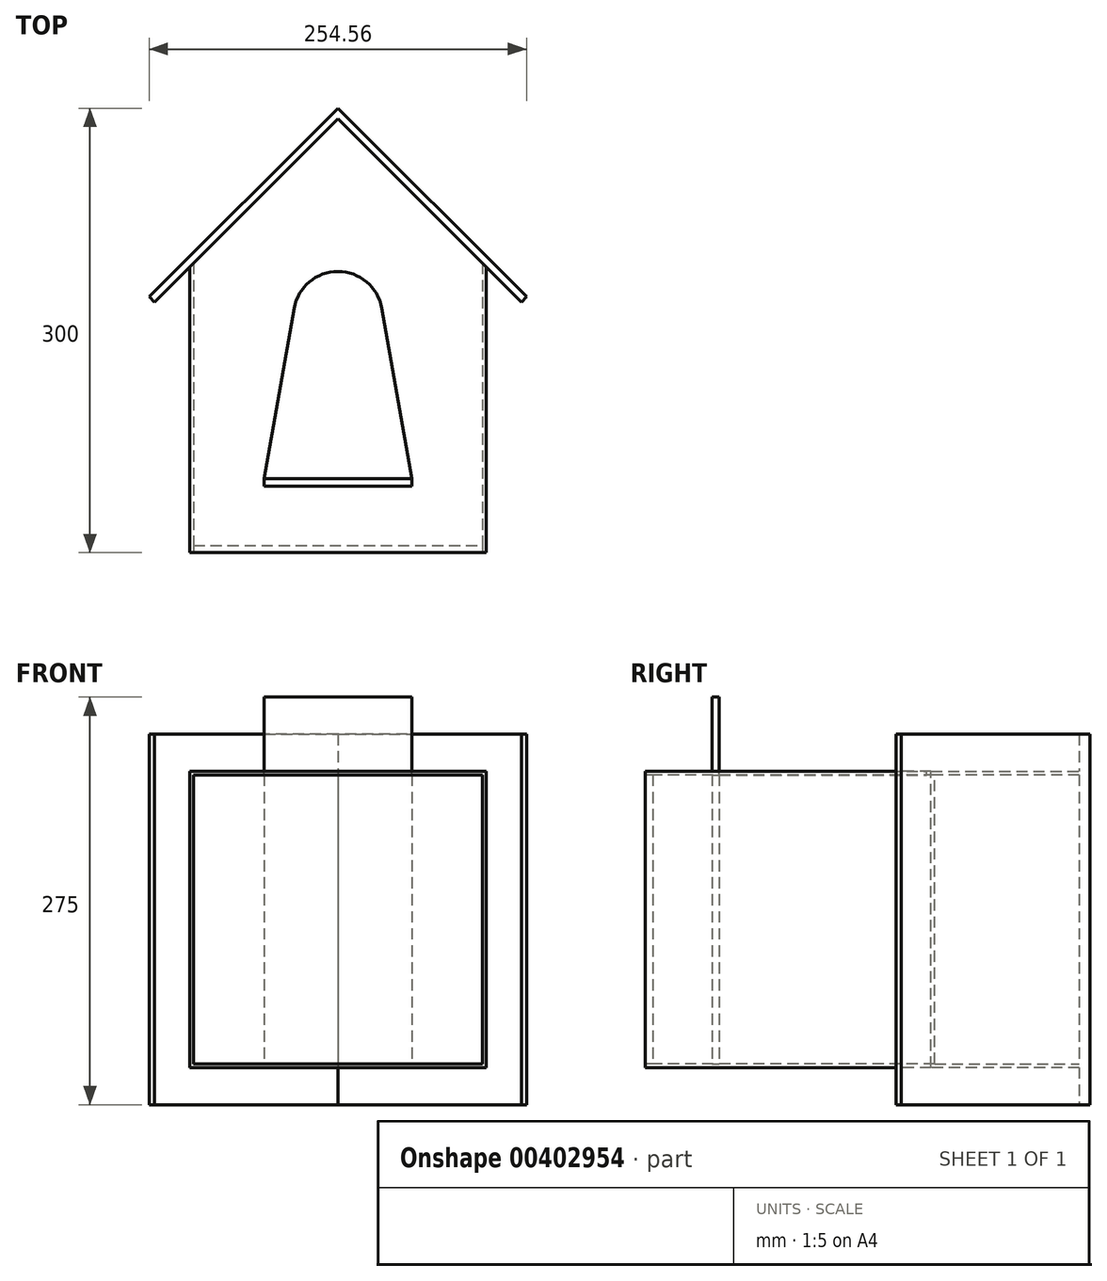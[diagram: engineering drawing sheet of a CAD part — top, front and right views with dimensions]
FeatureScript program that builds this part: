
annotation { "Feature Type Name" : "Feature", "Feature Type Description" : "" }
export const myFeature = defineFeature(function(context is Context, id is Id, definition is map)
    precondition{}
    {
        {
            var Q0;
            Q0=qCreatedBy(makeId("Top.planeOp"),FACE);
            var sketch = newSketch(context, id + "F0", { "sketchPlane" : qUnion([Q0])});
            skLineSegment(sketch, "E0.bottom", {"start": v(0, 0) * mm, "end": v(200, 0) * mm});
            skLineSegment(sketch, "E0.left", {"start": v(0, 200) * mm, "end": v(0, 0) * mm});
            skLineSegment(sketch, "E0.right", {"start": v(200, 200) * mm, "end": v(200, 0) * mm});
            skLineSegment(sketch, "E1", {"start": v(0, 200) * mm, "end": v(100, 300) * mm});
            skLineSegment(sketch, "E2", {"start": v(100, 300) * mm, "end": v(200, 200) * mm});
            skLineSegment(sketch, "E3", {"start": v(100, 300) * mm, "end": v(100, 0) * mm, "construction": true});
            skSolve(sketch);
        }
        {
            var Q0;
            Q0 = qSketchRegion(id + "F0", true);
            extrude(context, id + "F1", {"entities" : qUnion([Q0]), "depth" : 200 * mm});
        }
        {
            var Q0;
            Q0=makeQuery(id+"F1.opExtrude","SWEPT_FACE",FACE,{"disambiguationData":[OSD([sQuery(id+"F0.wireOp",EDGE,"E0.bottom")])]});
            shell(context, id + "F2", {"entities" : qUnion([Q0]), "thickness" : 2.5 * mm});
        }
        {
            var Q0;
            Q0=makeQuery(id+"F1.opExtrude","CAP_FACE",FACE,{"disambiguationData":[OSD([sQuery(id+"F0.wireOp",EDGE,"E0.bottom"),sQuery(id+"F0.wireOp",EDGE,"E0.left"),sQuery(id+"F0.wireOp",EDGE,"E0.right"),sQuery(id+"F0.wireOp",EDGE,"E1"),sQuery(id+"F0.wireOp",EDGE,"E2")])],"isStart":false});
            var sketch = newSketch(context, id + "F3", { "sketchPlane" : qUnion([Q0])});
            skLineSegment(sketch, "E4", {"start": v(100, 300) * mm, "end": v(-27.28, 172.72) * mm});
            skLineSegment(sketch, "E5", {"start": v(-27.28, 172.72) * mm, "end": v(-23.74, 169.19) * mm});
            skLineSegment(sketch, "E6", {"start": v(-23.74, 169.19) * mm, "end": v(100, 292.93) * mm});
            skLineSegment(sketch, "E7", {"start": v(100, 292.93) * mm, "end": v(223.74, 169.19) * mm});
            skLineSegment(sketch, "E8", {"start": v(223.74, 169.19) * mm, "end": v(227.28, 172.72) * mm});
            skLineSegment(sketch, "E9", {"start": v(227.28, 172.72) * mm, "end": v(100, 300) * mm});
            skSolve(sketch);
        }
        {
            var Q0;
            Q0 = qSketchRegion(id + "F3", true);
            extrude(context, id + "F4", {"entities" : qUnion([Q0]), "operationType" : NewBodyOperationType.ADD, "depth" : 25 * mm, "hasSecondDirection" : true, "secondDirectionOppositeDirection" : true, "secondDirectionDepth" : 225 * mm});
        }
        {
            var Q0;
            Q0=makeQuery(id+"F1.opExtrude","SWEPT_FACE",FACE,{"disambiguationData":[OSD([sQuery(id+"F0.wireOp",EDGE,"E0.bottom")])]});
            var sketch = newSketch(context, id + "F5", { "sketchPlane" : qUnion([Q0])});
            skLineSegment(sketch, "E10.bottom", {"start": v(2.5, 197.5) * mm, "end": v(197.5, 197.5) * mm});
            skLineSegment(sketch, "E10.top", {"start": v(2.5, 2.5) * mm, "end": v(197.5, 2.5) * mm});
            skLineSegment(sketch, "E10.left", {"start": v(2.5, 197.5) * mm, "end": v(2.5, 2.5) * mm});
            skLineSegment(sketch, "E10.right", {"start": v(197.5, 197.5) * mm, "end": v(197.5, 2.5) * mm});
            skSolve(sketch);
        }
        {
            var Q0;
            Q0 = qSketchRegion(id + "F5", true);
            extrude(context, id + "F6", {"entities" : qUnion([Q0]), "oppositeDirection" : true, "depth" : 5 * mm});
        }
        {
            var Q0;
            Q0=makeQuery(id+"F1.opExtrude","CAP_FACE",FACE,{"disambiguationData":[OSD([sQuery(id+"F0.wireOp",EDGE,"E0.bottom"),sQuery(id+"F0.wireOp",EDGE,"E0.left"),sQuery(id+"F0.wireOp",EDGE,"E0.right"),sQuery(id+"F0.wireOp",EDGE,"E1"),sQuery(id+"F0.wireOp",EDGE,"E2")])],"isStart":false});
            var sketch = newSketch(context, id + "F7", { "sketchPlane" : qUnion([Q0])});
            skArc(sketch, "E11", {"start": v(129.54, 165) * mm, "mid": v(100, 189.8) * mm, "end": v(70.46, 165) * mm});
            skLineSegment(sketch, "E12", {"start": v(70.46, 165) * mm, "end": v(50.18, 50) * mm});
            skLineSegment(sketch, "E13", {"start": v(50.18, 50) * mm, "end": v(149.82, 50) * mm});
            skLineSegment(sketch, "E14", {"start": v(149.82, 50) * mm, "end": v(129.54, 165) * mm});
            skLineSegment(sketch, "E15", {"start": v(129.54, 165) * mm, "end": v(70.46, 165) * mm, "construction": true});
            skLineSegment(sketch, "E16", {"start": v(100, 0) * mm, "end": v(100, 50) * mm, "construction": true});
            skSolve(sketch);
        }
        {
            var Q0;
            Q0 = qSketchRegion(id + "F7", true);
            extrude(context, id + "F8", {"entities" : qUnion([Q0]), "operationType" : NewBodyOperationType.REMOVE, "oppositeDirection" : true, "depth" : 25 * mm});
        }
        {
            var Q0;
            Q0=makeQuery(id+"F1.opExtrude","CAP_FACE",FACE,{"disambiguationData":[OSD([sQuery(id+"F0.wireOp",EDGE,"E0.bottom"),sQuery(id+"F0.wireOp",EDGE,"E0.left"),sQuery(id+"F0.wireOp",EDGE,"E0.right"),sQuery(id+"F0.wireOp",EDGE,"E1"),sQuery(id+"F0.wireOp",EDGE,"E2")])],"isStart":false});
            var sketch = newSketch(context, id + "F9", { "sketchPlane" : qUnion([Q0])});
            skLineSegment(sketch, "E17.bottom", {"start": v(50.18, 50) * mm, "end": v(149.82, 50) * mm});
            skLineSegment(sketch, "E17.top", {"start": v(50.18, 45) * mm, "end": v(149.82, 45) * mm});
            skLineSegment(sketch, "E17.left", {"start": v(50.18, 50) * mm, "end": v(50.18, 45) * mm});
            skLineSegment(sketch, "E17.right", {"start": v(149.82, 50) * mm, "end": v(149.82, 45) * mm});
            skSolve(sketch);
        }
        {
            var Q0;
            Q0 = qSketchRegion(id + "F9", true);
            extrude(context, id + "F10", {"entities" : qUnion([Q0]), "operationType" : NewBodyOperationType.ADD, "depth" : 50 * mm, "hasSecondDirection" : true, "secondDirectionOppositeDirection" : true, "secondDirectionDepth" : 200 * mm});
        }
    });
